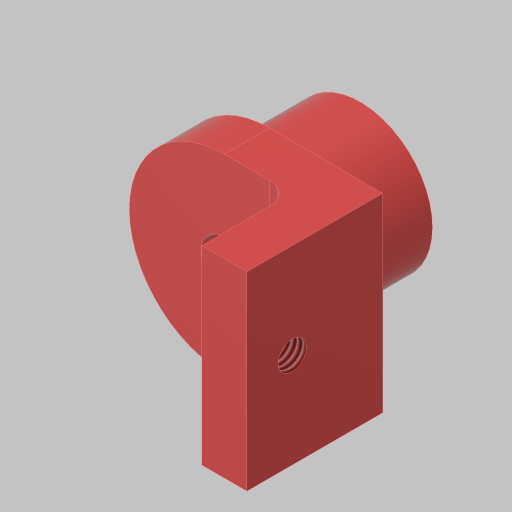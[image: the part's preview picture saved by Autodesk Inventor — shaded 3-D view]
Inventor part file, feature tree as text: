
AUTODESK INVENTOR PART (.ipt)
format: ipt  version: 2023.5 (Build 275446000, 446)  size: 145,920 bytes
history: native  units: in
note: dims shown in document units (in); Inventor stores cm internally (conversion verified against a paired STEP export)
features: sketch x5, extrude x3, hole x2, fillet x1, projected_geometry x1
ambient origin geometry x8: Origin, YZ Plane, XZ Plane, XY Plane, X Axis, Y Axis, Z Axis, Center Point
bodies: Solid1 (feature_tree)
feature tree (12):
  extrude  "Extrusion1"  Depth=0.5in TaperAngle=0.0deg
  extrude  "Extrusion2"  Depth=0.25in TaperAngle=0.0deg
  hole  "Hole2"  [1 undecoded]
  extrude  "Extrusion3"  Depth=0.25in
  fillet  "Fillet1"  Radius=0.5in
  hole  "Hole3"  [1 undecoded]
  sketch  "Sketch1"  dims[d0=0.8in d1=0.5in d2=0.0in]
  sketch  "Sketch2"  dims[d3=0.125in d4=0.25in d5=0.0in]
  sketch  "Sketch4"  dims[d6=0.688in d14=0.625in]
  sketch  "Sketch5"  dims[d15=0.257in d16=0.75in d17=0.375in d18=0.25in d19=0.5635in d20=1.0in d21=0.8108in d22=0.25in d23=0.5in d24=0.0in]
  sketch  "Sketch6"  dims[d25=0.125in d27=0.156in d28=0.38in d29=0.385in d30=0.25in d31=0.5635in d32=1.0in d33=0.8108in d35=0.25in]
  projected_geometry  "Project Cut Edges1"
note: 2 required parameter values undecoded (feature->parameter linkage not recoverable at this tier; creation-order binding heuristic only, values carry confidence <= 0.55)
